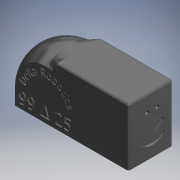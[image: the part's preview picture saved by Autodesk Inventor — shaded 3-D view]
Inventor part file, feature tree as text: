
AUTODESK INVENTOR PART (.ipt)
format: ipt  version: 2019 (Build 230136000, 136)  size: 941,056 bytes
history: native  units: mm (DEFAULTED — no unit token found)
features: sketch x16, extrude x15, plane x2, other x2, mirror x1, revolve x1, loft x1, fillet x1
ambient origin geometry x8: Origin, YZ Plane, XZ Plane, XY Plane, X Axis, Y Axis, Z Axis, Center Point
bodies: Solid1 (feature_tree)
feature tree (39):
  extrude  "Extrusion1"  Depth=88.9mm
  extrude  "Extrusion2"  Depth=25.4mm
  extrude  "Extrusion3"  Depth=3.175mm TaperAngle=0.0deg
  plane  "Work Plane1"
  mirror  "Mirror1"
  plane  "Work Plane2"
  revolve  "Revolution1"  [1 undecoded]
  extrude  "Extrusion5"  Depth=44.45mm
  extrude  "Extrusion8"  TaperAngle=90.0deg  [1 undecoded]
  extrude  "Extrusion9"  Depth=38.1mm
  extrude  "Extrusion10"  Depth=1.5875mm TaperAngle=0.0deg
  extrude  "Extrusion11"  Depth=3.175mm
  extrude  "Extrusion12"  Depth=3.175mm
  extrude  "Extrusion13"  Depth=12.7mm
  extrude  "Extrusion14"  Depth=71.628mm
  extrude  "Extrusion15"  Depth=5.08mm TaperAngle=0.0deg
  loft  "Loft3"
  extrude  "Extrusion16"  Depth=6.35mm
  fillet  "Fillet2"  Radius=6.35mm
  extrude  "Extrusion17"  Depth=3.175mm
  extrude  "Extrusion18"  Depth=3.175mm
  sketch  "Sketch1"  dims[d0=82.55mm d1=88.9mm]
  sketch  "Sketch2"  dims[d2=25.4mm d3=25.4mm]
  sketch  "Sketch3"  dims[d4=59.69mm d5=0.0mm d6=3.175mm d7=0.0mm]
  sketch  "Sketch5"  dims[d8=12.7mm d9=25.4mm]
  sketch  "Sketch8"  dims[d10=9.525mm d11=0.0mm d12=44.45mm]
  sketch  "Sketch10"  dims[d13=44.45mm d14=90.0deg]
  sketch  "Sketch11"  dims[d23=2.54mm d24=0.0mm d33=38.1mm]
  sketch  "Sketch13"  dims[d34=1.27mm d35=0.0mm d36=1.5875mm d37=0.0mm]
  sketch  "Sketch15"  dims[d38=3.175mm d39=3.175mm]
  sketch  "Sketch16"  dims[d40=3.175mm d41=19.05mm]
  sketch  "Sketch17"  dims[d42=12.7mm d43=12.7mm]
  sketch  "Sketch19"  dims[d44=12.7mm d46=71.628mm]
  sketch  "Sketch20"  dims[d47=25.4mm d48=0.0mm d53=5.08mm d54=0.0mm]
  other  "Edges4"
  other  "Edges5"
  sketch  "Sketch21"  dims[d55=25.4mm d56=0.0mm d57=3.048mm]
  sketch  "Sketch22"  dims[d58=3.048mm d59=6.35mm d60=6.35mm]
  sketch  "Sketch23"  dims[d61=8.001mm d62=6.477mm d63=24.003mm d64=25.4mm d65=0.0mm d72=55.88mm d73=0.0mm d78=62.865mm d79=0.0mm d80=0.0mm d81=90.0deg d82=0.0mm d83=90.0deg d84=3.175mm d85=6.35mm d86=6.35mm d87=6.35mm d88=6.35mm d89=74.93mm d90=0.0mm d91=3.175mm d92=74.93mm d93=0.0mm d94=3.175mm d95=0.0mm]
note: 2 required parameter values undecoded (feature->parameter linkage not recoverable at this tier; creation-order binding heuristic only, values carry confidence <= 0.55)